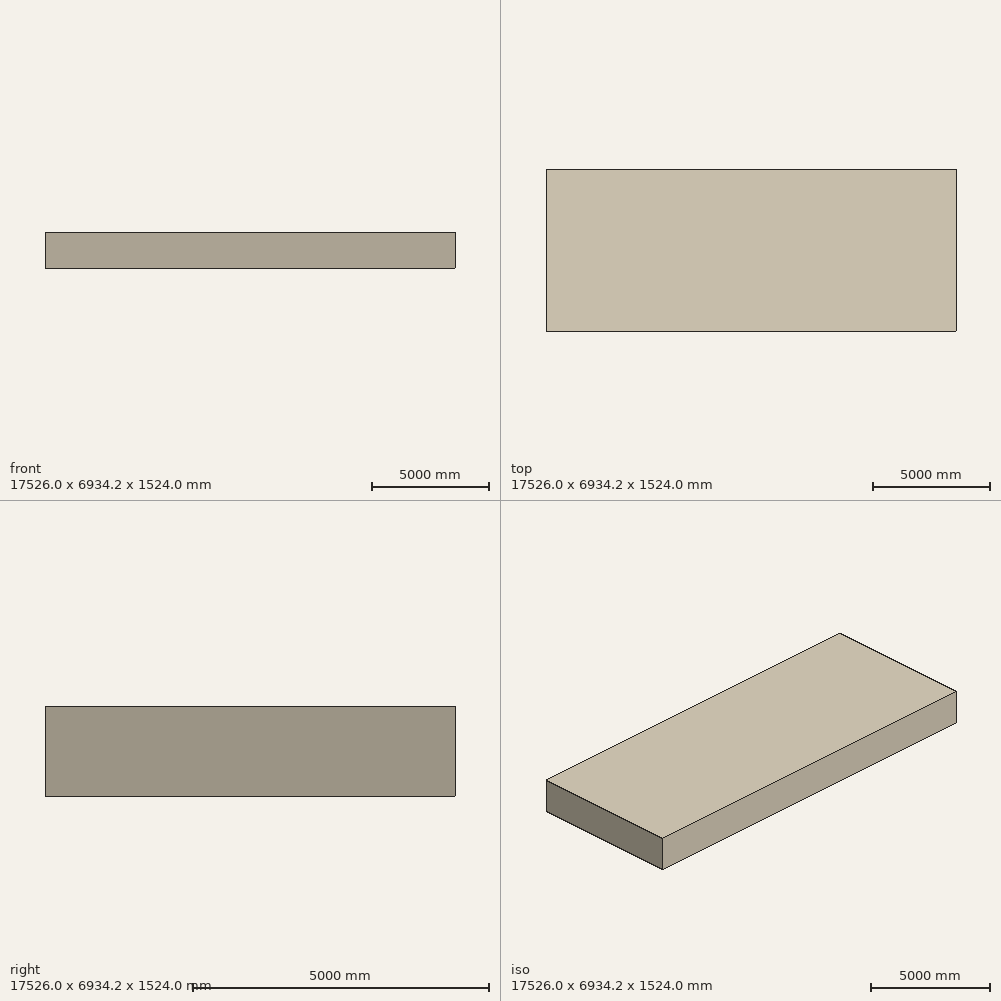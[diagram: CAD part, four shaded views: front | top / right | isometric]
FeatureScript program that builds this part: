
annotation { "Feature Type Name" : "Feature", "Feature Type Description" : "" }
export const myFeature = defineFeature(function(context is Context, id is Id, definition is map)
    precondition{}
    {
        {
            var Q0;
            Q0=qCreatedBy(makeId("Front.planeOp"),FACE);
            var sketch = newSketch(context, id + "F0", { "sketchPlane" : qUnion([Q0])});
            skLineSegment(sketch, "E0.bottom", {"start": v(0, 0) * mm, "end": v(17526, 0) * mm});
            skLineSegment(sketch, "E0.top", {"start": v(0, 1524) * mm, "end": v(17526, 1524) * mm});
            skLineSegment(sketch, "E0.left", {"start": v(0, 0) * mm, "end": v(0, 1524) * mm});
            skLineSegment(sketch, "E0.right", {"start": v(17526, 0) * mm, "end": v(17526, 1524) * mm});
            skSolve(sketch);
        }
        {
            var Q0;
            Q0 = qSketchRegion(id + "F0", true);
            extrude(context, id + "F1", {"entities" : qUnion([Q0]), "depth" : 6934.2 * mm});
        }
    });
